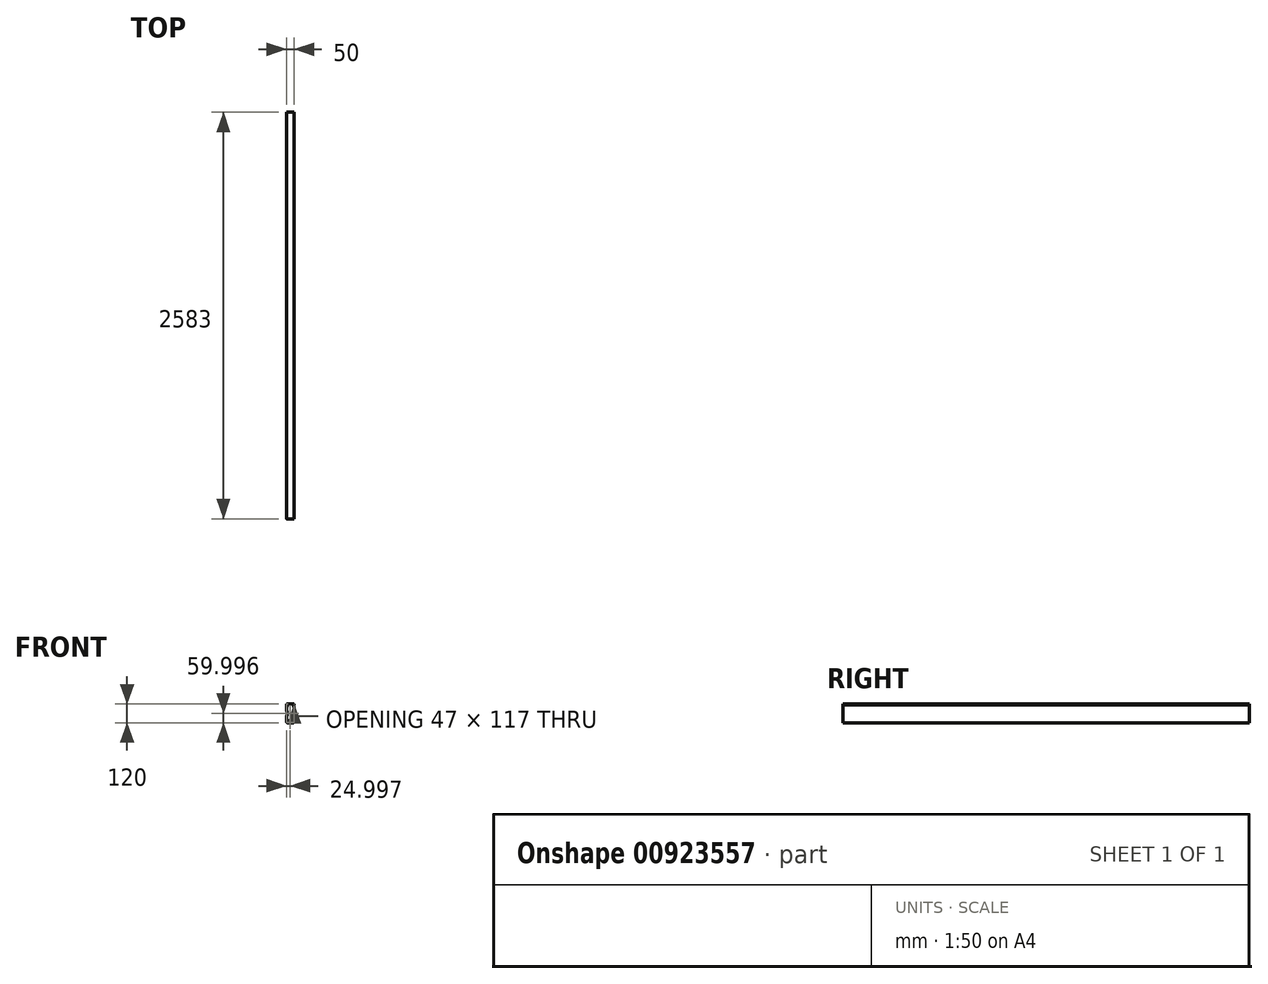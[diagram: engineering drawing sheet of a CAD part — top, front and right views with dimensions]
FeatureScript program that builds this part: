
annotation { "Feature Type Name" : "Feature", "Feature Type Description" : "" }
export const myFeature = defineFeature(function(context is Context, id is Id, definition is map)
    precondition{}
    {
        {
            var Q0;
            Q0=qCreatedBy(makeId("Front.planeOp"),FACE);
            var sketch = newSketch(context, id + "F0", { "sketchPlane" : qUnion([Q0])});
            skArc(sketch, "E0.filletArc", {"start": v(-76.42, 85.7) * mm, "mid": v(-80.94, 84.2) * mm, "end": v(-83.63, 80.26) * mm});
            skArc(sketch, "E1.filletArc", {"start": v(-83.63, -26.8) * mm, "mid": v(-81.44, -32.1) * mm, "end": v(-76.13, -34.3) * mm});
            skArc(sketch, "E2", {"start": v(-80.87, -20.14) * mm, "mid": v(-82.91, -23.2) * mm, "end": v(-83.63, -26.8) * mm});
            skArc(sketch, "E3", {"start": v(-80.03, -17.47) * mm, "mid": v(-80.97, -14.8) * mm, "end": v(-82.7, -12.57) * mm});
            skArc(sketch, "E4.filletArc", {"start": v(-80.87, -20.14) * mm, "mid": v(-80.12, -18.91) * mm, "end": v(-80.03, -17.47) * mm});
            skLineSegment(sketch, "E5", {"start": v(-83.63, -10.39) * mm, "end": v(-83.63, 8.51) * mm});
            skLineSegment(sketch, "E6", {"start": v(-83.63, 10.7) * mm, "end": v(-83.63, 10.7) * mm});
            skLineSegment(sketch, "E7", {"start": v(-80.63, 13.7) * mm, "end": v(-80.63, 37.7) * mm});
            skLineSegment(sketch, "E8", {"start": v(-83.63, 40.7) * mm, "end": v(-83.63, 40.7) * mm});
            skArc(sketch, "E9.filletArc", {"start": v(-82.13, 11.1) * mm, "mid": v(-81.03, 12.2) * mm, "end": v(-80.63, 13.7) * mm});
            skPoint(sketch, "E10.visualSharp", {"position": v(-83.63, 10.7) * mm});
            skArc(sketch, "E10.filletArc", {"start": v(-82.13, 11.1) * mm, "mid": v(-83.23, 10.01) * mm, "end": v(-83.63, 8.51) * mm});
            skArc(sketch, "E11.filletArc", {"start": v(-80.63, 37.7) * mm, "mid": v(-81.03, 39.2) * mm, "end": v(-82.13, 40.3) * mm});
            skPoint(sketch, "E12.visualSharp", {"position": v(-83.63, 40.7) * mm});
            skArc(sketch, "E12.filletArc", {"start": v(-83.63, 42.9) * mm, "mid": v(-83.23, 41.4) * mm, "end": v(-82.13, 40.3) * mm});
            skArc(sketch, "E13.filletArc", {"start": v(-83.63, -10.39) * mm, "mid": v(-83.39, -11.58) * mm, "end": v(-82.7, -12.57) * mm});
            skArc(sketch, "E14", {"start": v(-83.63, 80.26) * mm, "mid": v(-82.92, 76.67) * mm, "end": v(-80.89, 73.63) * mm});
            skArc(sketch, "E15", {"start": v(-82.72, 66.04) * mm, "mid": v(-81.02, 68.28) * mm, "end": v(-80.07, 70.92) * mm});
            skArc(sketch, "E16.filletArc", {"start": v(-80.07, 70.92) * mm, "mid": v(-80.14, 72.38) * mm, "end": v(-80.89, 73.63) * mm});
            skArc(sketch, "E17.filletArc", {"start": v(-82.72, 66.04) * mm, "mid": v(-83.4, 65.05) * mm, "end": v(-83.63, 63.88) * mm});
            skLineSegment(sketch, "E18", {"start": v(-83.63, 42.9) * mm, "end": v(-83.63, 63.88) * mm});
            skArc(sketch, "E19.MirrorCS", {"start": v(-33.63, 42.9) * mm, "mid": v(-34.03, 41.4) * mm, "end": v(-35.13, 40.3) * mm});
            skArc(sketch, "E20.MirrorCS", {"start": v(-36.63, 37.7) * mm, "mid": v(-36.23, 39.2) * mm, "end": v(-35.13, 40.3) * mm});
            skArc(sketch, "E21.MirrorCS", {"start": v(-35.13, 11.1) * mm, "mid": v(-36.23, 12.2) * mm, "end": v(-36.63, 13.7) * mm});
            skArc(sketch, "E22.MirrorCS", {"start": v(-35.13, 11.1) * mm, "mid": v(-34.03, 10.01) * mm, "end": v(-33.63, 8.51) * mm});
            skArc(sketch, "E23.MirrorCS", {"start": v(-34.54, 66.04) * mm, "mid": v(-33.87, 65.05) * mm, "end": v(-33.63, 63.88) * mm});
            skArc(sketch, "E24.MirrorCS", {"start": v(-36.4, -20.14) * mm, "mid": v(-37.15, -18.91) * mm, "end": v(-37.24, -17.47) * mm});
            skArc(sketch, "E25.MirrorCS", {"start": v(-33.63, -10.39) * mm, "mid": v(-33.88, -11.58) * mm, "end": v(-34.57, -12.57) * mm});
            skArc(sketch, "E26.MirrorCS", {"start": v(-37.2, 70.92) * mm, "mid": v(-37.13, 72.38) * mm, "end": v(-36.38, 73.63) * mm});
            skArc(sketch, "E27.MirrorCS", {"start": v(-34.54, 66.04) * mm, "mid": v(-36.24, 68.28) * mm, "end": v(-37.2, 70.92) * mm});
            skArc(sketch, "E28.MirrorCS", {"start": v(-37.24, -17.47) * mm, "mid": v(-36.3, -14.8) * mm, "end": v(-34.57, -12.57) * mm});
            skArc(sketch, "E29.MirrorCS", {"start": v(-33.63, 80.26) * mm, "mid": v(-34.35, 76.67) * mm, "end": v(-36.38, 73.63) * mm});
            skArc(sketch, "E30.MirrorCS", {"start": v(-36.4, -20.14) * mm, "mid": v(-34.35, -23.2) * mm, "end": v(-33.63, -26.8) * mm});
            skArc(sketch, "E31.MirrorCS", {"start": v(-33.63, -26.8) * mm, "mid": v(-35.83, -32.1) * mm, "end": v(-41.13, -34.3) * mm});
            skArc(sketch, "E32.MirrorCS", {"start": v(-40.85, 85.7) * mm, "mid": v(-36.33, 84.2) * mm, "end": v(-33.63, 80.26) * mm});
            skLineSegment(sketch, "E33.MirrorCS", {"start": v(-33.63, 42.9) * mm, "end": v(-33.63, 63.88) * mm});
            skLineSegment(sketch, "E34.MirrorCS", {"start": v(-33.63, -10.39) * mm, "end": v(-33.63, 8.51) * mm});
            skLineSegment(sketch, "E35.MirrorCS", {"start": v(-36.63, 13.7) * mm, "end": v(-36.63, 37.7) * mm});
            skLineSegment(sketch, "E36", {"start": v(-76.42, 85.7) * mm, "end": v(-40.85, 85.7) * mm});
            skLineSegment(sketch, "E37", {"start": v(-76.13, -34.3) * mm, "end": v(-41.13, -34.3) * mm});
            skSolve(sketch);
        }
        {
            var Q0;
            Q0=makeQuery(id+"F0.imprint","IMPRINT",FACE,{"disambiguationData":[TD([[makeQuery(id+"F0.imprint","IMPRINT",EDGE,{"derivedFrom":sQuery(id+"F0.wireOp",EDGE,"E0.filletArc")}),1.0]])]});
            extrude(context, id + "F1", {"entities" : qUnion([Q0]), "depth" : 2583 * mm, "offsetDistance" : 25 * mm});
        }
        {
            var Q0;
            Q0=makeQuery(id+"F1.opExtrude","CAP_FACE",FACE,{"disambiguationData":[OSD([sQuery(id+"F0.wireOp",EDGE,"E0.filletArc"),sQuery(id+"F0.wireOp",EDGE,"E1.filletArc"),sQuery(id+"F0.wireOp",EDGE,"E2"),sQuery(id+"F0.wireOp",EDGE,"E3"),sQuery(id+"F0.wireOp",EDGE,"E4.filletArc"),sQuery(id+"F0.wireOp",EDGE,"E5"),sQuery(id+"F0.wireOp",EDGE,"E7"),sQuery(id+"F0.wireOp",EDGE,"E9.filletArc"),sQuery(id+"F0.wireOp",EDGE,"E10.filletArc"),sQuery(id+"F0.wireOp",EDGE,"E11.filletArc"),sQuery(id+"F0.wireOp",EDGE,"E12.filletArc"),sQuery(id+"F0.wireOp",EDGE,"E13.filletArc"),sQuery(id+"F0.wireOp",EDGE,"E14"),sQuery(id+"F0.wireOp",EDGE,"E15"),sQuery(id+"F0.wireOp",EDGE,"E16.filletArc"),sQuery(id+"F0.wireOp",EDGE,"E17.filletArc"),sQuery(id+"F0.wireOp",EDGE,"E18"),sQuery(id+"F0.wireOp",EDGE,"E19.MirrorCS"),sQuery(id+"F0.wireOp",EDGE,"E20.MirrorCS"),sQuery(id+"F0.wireOp",EDGE,"E21.MirrorCS"),sQuery(id+"F0.wireOp",EDGE,"E22.MirrorCS"),sQuery(id+"F0.wireOp",EDGE,"E23.MirrorCS"),sQuery(id+"F0.wireOp",EDGE,"E24.MirrorCS"),sQuery(id+"F0.wireOp",EDGE,"E25.MirrorCS"),sQuery(id+"F0.wireOp",EDGE,"E26.MirrorCS"),sQuery(id+"F0.wireOp",EDGE,"E27.MirrorCS"),sQuery(id+"F0.wireOp",EDGE,"E28.MirrorCS"),sQuery(id+"F0.wireOp",EDGE,"E29.MirrorCS"),sQuery(id+"F0.wireOp",EDGE,"E30.MirrorCS"),sQuery(id+"F0.wireOp",EDGE,"E31.MirrorCS"),sQuery(id+"F0.wireOp",EDGE,"E32.MirrorCS"),sQuery(id+"F0.wireOp",EDGE,"E33.MirrorCS"),sQuery(id+"F0.wireOp",EDGE,"E34.MirrorCS"),sQuery(id+"F0.wireOp",EDGE,"E35.MirrorCS"),sQuery(id+"F0.wireOp",EDGE,"E36"),sQuery(id+"F0.wireOp",EDGE,"E37")])],"isStart":false});
            var Q1;
            Q1=makeQuery(id+"F1.opExtrude","CAP_FACE",FACE,{"disambiguationData":[OSD([sQuery(id+"F0.wireOp",EDGE,"E0.filletArc"),sQuery(id+"F0.wireOp",EDGE,"E1.filletArc"),sQuery(id+"F0.wireOp",EDGE,"E2"),sQuery(id+"F0.wireOp",EDGE,"E3"),sQuery(id+"F0.wireOp",EDGE,"E4.filletArc"),sQuery(id+"F0.wireOp",EDGE,"E5"),sQuery(id+"F0.wireOp",EDGE,"E7"),sQuery(id+"F0.wireOp",EDGE,"E9.filletArc"),sQuery(id+"F0.wireOp",EDGE,"E10.filletArc"),sQuery(id+"F0.wireOp",EDGE,"E11.filletArc"),sQuery(id+"F0.wireOp",EDGE,"E12.filletArc"),sQuery(id+"F0.wireOp",EDGE,"E13.filletArc"),sQuery(id+"F0.wireOp",EDGE,"E14"),sQuery(id+"F0.wireOp",EDGE,"E15"),sQuery(id+"F0.wireOp",EDGE,"E16.filletArc"),sQuery(id+"F0.wireOp",EDGE,"E17.filletArc"),sQuery(id+"F0.wireOp",EDGE,"E18"),sQuery(id+"F0.wireOp",EDGE,"E19.MirrorCS"),sQuery(id+"F0.wireOp",EDGE,"E20.MirrorCS"),sQuery(id+"F0.wireOp",EDGE,"E21.MirrorCS"),sQuery(id+"F0.wireOp",EDGE,"E22.MirrorCS"),sQuery(id+"F0.wireOp",EDGE,"E23.MirrorCS"),sQuery(id+"F0.wireOp",EDGE,"E24.MirrorCS"),sQuery(id+"F0.wireOp",EDGE,"E25.MirrorCS"),sQuery(id+"F0.wireOp",EDGE,"E26.MirrorCS"),sQuery(id+"F0.wireOp",EDGE,"E27.MirrorCS"),sQuery(id+"F0.wireOp",EDGE,"E28.MirrorCS"),sQuery(id+"F0.wireOp",EDGE,"E29.MirrorCS"),sQuery(id+"F0.wireOp",EDGE,"E30.MirrorCS"),sQuery(id+"F0.wireOp",EDGE,"E31.MirrorCS"),sQuery(id+"F0.wireOp",EDGE,"E32.MirrorCS"),sQuery(id+"F0.wireOp",EDGE,"E33.MirrorCS"),sQuery(id+"F0.wireOp",EDGE,"E34.MirrorCS"),sQuery(id+"F0.wireOp",EDGE,"E35.MirrorCS"),sQuery(id+"F0.wireOp",EDGE,"E36"),sQuery(id+"F0.wireOp",EDGE,"E37")])],"isStart":true});
            shell(context, id + "F2", {"entities" : qUnion([Q0, Q1]), "thickness" : 1.5 * mm});
        }
    });
